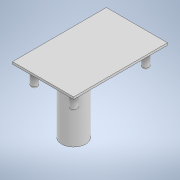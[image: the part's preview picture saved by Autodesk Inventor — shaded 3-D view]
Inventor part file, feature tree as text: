
AUTODESK INVENTOR PART (.ipt)
format: ipt  version: 2021 (Build 250183000, 183)  size: 151,040 bytes
history: native  units: mm
features: extrude x3, sketch x3, fillet x2, other x1, chamfer x1
ambient origin geometry x8: Origin, YZ Plane, XZ Plane, XY Plane, X Axis, Y Axis, Z Axis, Center Point
bodies: Body1 (feature_tree)
feature tree (10):
  other  "Sólido1"
  extrude  "Extrusión1"  Depth=18.0mm
  extrude  "Extrusión2"  Depth=3.0mm
  extrude  "Extrusión3"  Depth=3.0mm
  fillet  "Empalme1"  Radius=5.0mm
  fillet  "Empalme2"  Radius=5.0mm
  chamfer  "Chaflán1"  Distance=43.0mm
  sketch  "Boceto1"  dims[d0=33.0mm d1=18.0mm]
  sketch  "Boceto2"  dims[d2=3.0mm d3=3.0mm]
  sketch  "Boceto3"  dims[d4=3.0mm d5=3.0mm d6=5.0mm d7=5.0mm d8=43.0mm d9=5.0mm d10=9.0mm d11=11.0mm d12=3.0mm d13=0.0mm d14=30.0mm d15=0.0mm d16=10.0mm d17=0.0mm d18=1.0mm d19=1.0mm d20=2.0mm d21=2.0mm d22=45.0deg]
